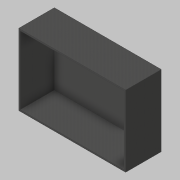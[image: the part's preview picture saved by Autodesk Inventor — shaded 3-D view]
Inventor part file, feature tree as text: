
AUTODESK INVENTOR PART (.ipt)
format: ipt  version: 2018.1 (Build 221168000, 168)  size: 117,760 bytes
history: native  units: in
note: dims shown in document units (in); Inventor stores cm internally (conversion verified against a paired STEP export)
features: extrude x2, sketch x1, plane x1
ambient origin geometry x8: Origin, YZ Plane, XZ Plane, XY Plane, X Axis, Y Axis, Z Axis, Center Point
bodies: Solid1 (feature_tree)
feature tree (4):
  sketch  "Sketch1"  dims[d0=24.0in d1=36.0in d2=0.5in d3=0.5in d4=0.5in d5=0.5in d6=12.0in d7=0.0in d8=0.5in d9=0.0in]
  extrude  "Extrusion1"  Depth=36.0in
  extrude  "Extrusion2"  Depth=0.5in
  plane  "Work Plane1"
